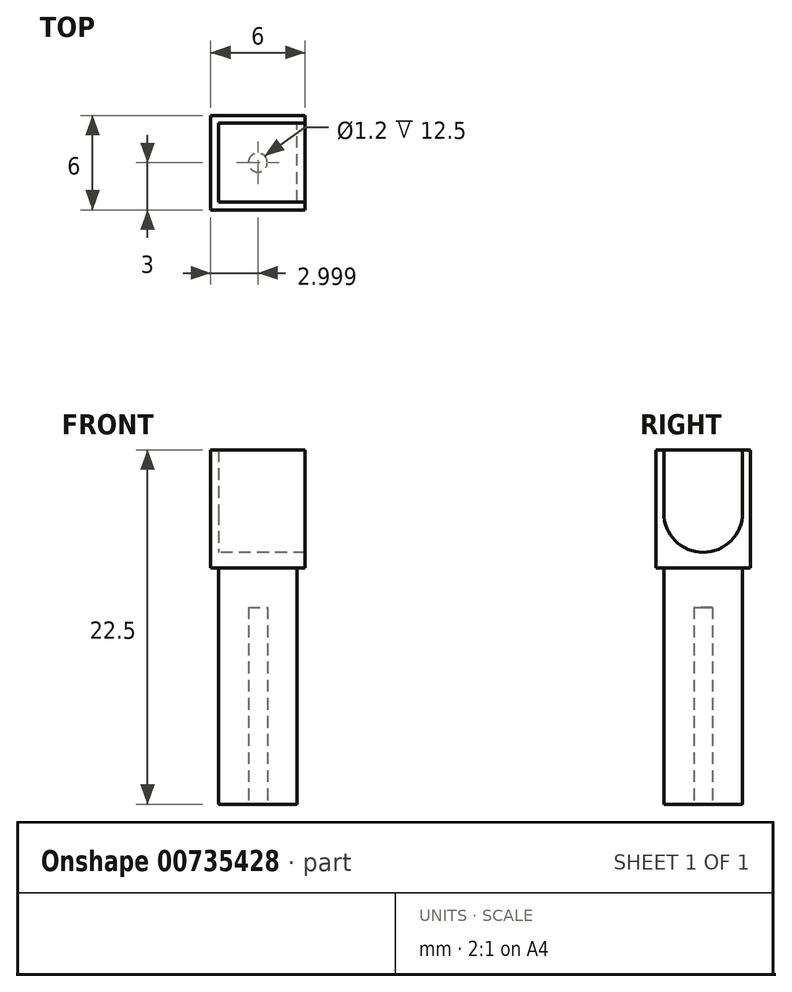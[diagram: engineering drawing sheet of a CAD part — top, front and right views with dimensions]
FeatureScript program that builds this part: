
annotation { "Feature Type Name" : "Feature", "Feature Type Description" : "" }
export const myFeature = defineFeature(function(context is Context, id is Id, definition is map)
    precondition{}
    {
        {
            var Q0;
            Q0=qCreatedBy(makeId("Front.planeOp"),FACE);
            var sketch = newSketch(context, id + "F0", { "sketchPlane" : qUnion([Q0])});
            skLineSegment(sketch, "E0.bottom", {"start": v(-3.25, 14.3) * mm, "end": v(1.75, 14.3) * mm});
            skLineSegment(sketch, "E0.top", {"start": v(-3.25, -8.2) * mm, "end": v(1.75, -8.2) * mm});
            skLineSegment(sketch, "E0.left", {"start": v(-3.25, 14.3) * mm, "end": v(-3.25, -8.2) * mm});
            skLineSegment(sketch, "E0.right", {"start": v(1.75, 14.3) * mm, "end": v(1.75, -8.2) * mm});
            skSolve(sketch);
        }
        {
            var Q0;
            Q0=makeQuery(id+"F0.imprint","IMPRINT",FACE,{"disambiguationData":[TD([[makeQuery(id+"F0.imprint","IMPRINT",EDGE,{"derivedFrom":sQuery(id+"F0.wireOp",EDGE,"E0.bottom")}),-1.0]])]});
            extrude(context, id + "F1", {"entities" : qUnion([Q0]), "depth" : 5 * mm, "offsetDistance" : 25 * mm});
        }
        {
            var Q0;
            Q0=makeQuery(id+"F1.opExtrude","SWEPT_FACE",FACE,{"disambiguationData":[OSD([sQuery(id+"F0.wireOp",EDGE,"E0.top")])]});
            var sketch = newSketch(context, id + "F2", { "sketchPlane" : qUnion([Q0])});
            skCircle(sketch, "E1", {"center": v(-0.75, 2.5) * mm, "radius": 0.6 * mm});
            skPoint(sketch, "E1.centerSnap0", {"position": v(-0.75, 5) * mm});
            skPoint(sketch, "E1.centerSnap1", {"position": v(-3.25, 2.5) * mm});
            skSolve(sketch);
        }
        {
            var Q0;
            Q0=makeQuery(id+"F2.imprint","IMPRINT",FACE,{"disambiguationData":[TD([[makeQuery(id+"F2.imprint","IMPRINT",EDGE,{"derivedFrom":sQuery(id+"F2.wireOp",EDGE,"E1")}),1.0]])]});
            extrude(context, id + "F3", {"entities" : qUnion([Q0]), "operationType" : NewBodyOperationType.REMOVE, "oppositeDirection" : true, "depth" : 20 * mm, "offsetDistance" : 25 * mm});
        }
        {
            var Q0;
            Q0=makeQuery(id+"F1.opExtrude","CAP_FACE",FACE,{"disambiguationData":[OSD([sQuery(id+"F0.wireOp",EDGE,"E0.bottom"),sQuery(id+"F0.wireOp",EDGE,"E0.top"),sQuery(id+"F0.wireOp",EDGE,"E0.left"),sQuery(id+"F0.wireOp",EDGE,"E0.right")])],"isStart":false});
            var sketch = newSketch(context, id + "F4", { "sketchPlane" : qUnion([Q0])});
            skLineSegment(sketch, "E2", {"start": v(-3.25, 14.3) * mm, "end": v(-3.25, 19.3) * mm});
            skLineSegment(sketch, "E3.bottom", {"start": v(-3.25, 19.3) * mm, "end": v(1.75, 19.3) * mm});
            skLineSegment(sketch, "E3.top", {"start": v(-3.25, 14.3) * mm, "end": v(1.75, 14.3) * mm});
            skLineSegment(sketch, "E3.left", {"start": v(-3.25, 19.3) * mm, "end": v(-3.25, 14.3) * mm});
            skLineSegment(sketch, "E3.right", {"start": v(1.75, 19.3) * mm, "end": v(1.75, 14.3) * mm});
            skSolve(sketch);
        }
        {
            var Q0;
            Q0=makeQuery(id+"F4.imprint","IMPRINT",FACE,{"disambiguationData":[TD([[makeQuery(id+"F4.imprint","IMPRINT",EDGE,{"derivedFrom":sQuery(id+"F4.wireOp",EDGE,"E3.bottom")}),-1.0]])]});
            extrude(context, id + "F5", {"entities" : qUnion([Q0]), "operationType" : NewBodyOperationType.ADD, "oppositeDirection" : true, "depth" : 5 * mm, "offsetDistance" : 25 * mm});
        }
        {
            var Q0;
            Q0=makeQuery(id+"F5.boolean.opBoolean","MERGE",FACE,{"derivedFrom":[makeQuery(id+"F1.opExtrude","SWEPT_FACE",FACE,{"disambiguationData":[OSD([sQuery(id+"F0.wireOp",EDGE,"E0.right")])]}),makeQuery(id+"F5.opExtrude","SWEPT_FACE",FACE,{"disambiguationData":[OSD([sQuery(id+"F4.wireOp",EDGE,"E3.right")])]})]});
            var sketch = newSketch(context, id + "F6", { "sketchPlane" : qUnion([Q0])});
            skLineSegment(sketch, "E4", {"start": v(0, 19.3) * mm, "end": v(0, 14.3) * mm});
            skLineSegment(sketch, "E5", {"start": v(0, 14.3) * mm, "end": v(-5, 14.3) * mm});
            skSolve(sketch);
        }
        {
            var Q0;
            Q0=makeQuery(id+"F6.imprint","IMPRINT",FACE,{"disambiguationData":[TD([[makeQuery(id+"F6.imprint","IMPRINT",EDGE,{"derivedFrom":sQuery(id+"F6.wireOp",EDGE,"E4")}),-1.0]])]});
            extrude(context, id + "F7", {"entities" : qUnion([Q0]), "operationType" : NewBodyOperationType.ADD, "depth" : 0.5 * mm, "offsetDistance" : 25 * mm});
        }
        {
            var Q0;
            Q0=makeQuery(id+"F7.boolean.opBoolean","MERGE",FACE,{"derivedFrom":[makeQuery(id+"F5.boolean.opBoolean","MERGE",FACE,{"derivedFrom":[makeQuery(id+"F1.opExtrude","CAP_FACE",FACE,{"disambiguationData":[OSD([sQuery(id+"F0.wireOp",EDGE,"E0.bottom"),sQuery(id+"F0.wireOp",EDGE,"E0.top"),sQuery(id+"F0.wireOp",EDGE,"E0.left"),sQuery(id+"F0.wireOp",EDGE,"E0.right")])],"isStart":true}),makeQuery(id+"F5.opExtrude","CAP_FACE",FACE,{"disambiguationData":[OSD([sQuery(id+"F4.wireOp",EDGE,"E3.bottom"),sQuery(id+"F4.wireOp",EDGE,"E3.top"),sQuery(id+"F4.wireOp",EDGE,"E3.left"),sQuery(id+"F4.wireOp",EDGE,"E3.right")])],"isStart":false})]}),makeQuery(id+"F7.opExtrude","SWEPT_FACE",FACE,{"disambiguationData":[OSD([sQuery(id+"F6.wireOp",EDGE,"E4")])]})]});
            var sketch = newSketch(context, id + "F8", { "sketchPlane" : qUnion([Q0])});
            skLineSegment(sketch, "E6", {"start": v(-1.75, 14.3) * mm, "end": v(3.25, 14.3) * mm});
            skSolve(sketch);
        }
        {
            var Q0;
            {var subQ4=sQuery(id+"F8.wireOp",EDGE,"E6");Q0=makeQuery(id+"F8.imprint","IMPRINT",FACE,{"disambiguationData":[TD([[makeQuery(id+"F8.imprint","IMPRINT",EDGE,{"derivedFrom":subQ4}),1.0]])]});}
            extrude(context, id + "F9", {"entities" : qUnion([Q0]), "operationType" : NewBodyOperationType.ADD, "depth" : 0.5 * mm, "offsetDistance" : 25 * mm});
        }
        {
            var Q0;
            {var subQ0=sQuery(id+"F4.wireOp",EDGE,"E3.right");var subQ1=sQuery(id+"F0.wireOp",EDGE,"E0.right");Q0=makeQuery(id+"F7.boolean.opBoolean","MERGE",FACE,{"derivedFrom":[makeQuery(id+"F5.boolean.opBoolean","MERGE",FACE,{"derivedFrom":[makeQuery(id+"F1.opExtrude","CAP_FACE",FACE,{"disambiguationData":[OSD([sQuery(id+"F0.wireOp",EDGE,"E0.bottom"),sQuery(id+"F0.wireOp",EDGE,"E0.top"),sQuery(id+"F0.wireOp",EDGE,"E0.left"),subQ1])],"isStart":false}),makeQuery(id+"F5.opExtrude","CAP_FACE",FACE,{"disambiguationData":[OSD([sQuery(id+"F4.wireOp",EDGE,"E3.bottom"),sQuery(id+"F4.wireOp",EDGE,"E3.top"),sQuery(id+"F4.wireOp",EDGE,"E3.left"),subQ0])],"isStart":true})]}),makeQuery(id+"F7.opExtrude","SWEPT_FACE",FACE,{"disambiguationData":[OSD([subQ1,subQ0])]})]});}
            var sketch = newSketch(context, id + "F10", { "sketchPlane" : qUnion([Q0])});
            skLineSegment(sketch, "E7", {"start": v(1.75, 14.3) * mm, "end": v(-3.25, 14.3) * mm});
            skSolve(sketch);
        }
        {
            var Q0;
            {var subQ4=sQuery(id+"F10.wireOp",EDGE,"E7");Q0=makeQuery(id+"F10.imprint","IMPRINT",FACE,{"disambiguationData":[TD([[makeQuery(id+"F10.imprint","IMPRINT",EDGE,{"derivedFrom":subQ4}),-1.0]])]});}
            extrude(context, id + "F11", {"entities" : qUnion([Q0]), "operationType" : NewBodyOperationType.ADD, "depth" : 0.5 * mm, "offsetDistance" : 25 * mm});
        }
        {
            var Q0;
            {var subQ0=sQuery(id+"F4.wireOp",EDGE,"E3.left");var subQ1=sQuery(id+"F0.wireOp",EDGE,"E0.left");Q0=makeQuery(id+"F11.boolean.opBoolean","MERGE",FACE,{"derivedFrom":[makeQuery(id+"F9.boolean.opBoolean","MERGE",FACE,{"derivedFrom":[makeQuery(id+"F5.boolean.opBoolean","MERGE",FACE,{"derivedFrom":[makeQuery(id+"F1.opExtrude","SWEPT_FACE",FACE,{"disambiguationData":[OSD([subQ1])]}),makeQuery(id+"F5.opExtrude","SWEPT_FACE",FACE,{"disambiguationData":[OSD([subQ0])]})]}),makeQuery(id+"F9.opExtrude","SWEPT_FACE",FACE,{"disambiguationData":[OSD([subQ1,subQ0])]})]}),makeQuery(id+"F11.opExtrude","SWEPT_FACE",FACE,{"disambiguationData":[OSD([subQ1,subQ0])]})]});}
            var sketch = newSketch(context, id + "F12", { "sketchPlane" : qUnion([Q0])});
            skLineSegment(sketch, "E8", {"start": v(0, 14.3) * mm, "end": v(5, 14.3) * mm});
            skSolve(sketch);
        }
        {
            var Q0;
            Q0=makeQuery(id+"F12.imprint","IMPRINT",FACE,{"disambiguationData":[TD([[makeQuery(id+"F12.imprint","IMPRINT",EDGE,{"derivedFrom":sQuery(id+"F12.wireOp",EDGE,"E8")}),1.0]])]});
            extrude(context, id + "F13", {"entities" : qUnion([Q0]), "operationType" : NewBodyOperationType.ADD, "depth" : 0.5 * mm, "offsetDistance" : 25 * mm});
        }
        {
            var Q0;
            Q0=makeQuery(id+"F13.opExtrude","CAP_FACE",FACE,{"disambiguationData":[OSD([sQuery(id+"F0.wireOp",EDGE,"E0.left"),sQuery(id+"F0.wireOp",EDGE,"E0.right"),sQuery(id+"F4.wireOp",EDGE,"E3.bottom"),sQuery(id+"F4.wireOp",EDGE,"E3.left"),sQuery(id+"F4.wireOp",EDGE,"E3.right"),sQuery(id+"F6.wireOp",EDGE,"E4"),sQuery(id+"F8.wireOp",EDGE,"E6"),sQuery(id+"F10.wireOp",EDGE,"E7"),sQuery(id+"F12.wireOp",EDGE,"E8")])],"isStart":false});
            var sketch = newSketch(context, id + "F14", { "sketchPlane" : qUnion([Q0])});
            skLineSegment(sketch, "E9", {"start": v(0, 17.8) * mm, "end": v(-0.5, 17.8) * mm});
            skLineSegment(sketch, "E10", {"start": v(5, 17.8) * mm, "end": v(5.5, 17.8) * mm});
            skArc(sketch, "E11", {"start": v(0, 17.8) * mm, "mid": v(2.5, 15.3) * mm, "end": v(5, 17.8) * mm});
            skSolve(sketch);
        }
        {
            var Q0;
            {var subQ4=sQuery(id+"F14.wireOp",EDGE,"E9");Q0=makeQuery(id+"F14.imprint","IMPRINT",FACE,{"disambiguationData":[TD([[makeQuery(id+"F14.imprint","IMPRINT",EDGE,{"derivedFrom":subQ4}),-1.0]])]});}
            extrude(context, id + "F15", {"entities" : qUnion([Q0]), "operationType" : NewBodyOperationType.REMOVE, "oppositeDirection" : true, "depth" : 25 * mm, "offsetDistance" : 25 * mm});
        }
        {
            var Q0;
            Q0=makeQuery(id+"F15.boolean.opBoolean","COPY",FACE,{"derivedFrom":makeQuery(id+"F15.opExtrude","SWEPT_FACE",FACE,{"disambiguationData":[OSD([sQuery(id+"F14.wireOp",EDGE,"E10")])]})});
            var Q1;
            Q1=makeQuery(id+"F15.boolean.opBoolean","COPY",FACE,{"derivedFrom":makeQuery(id+"F15.opExtrude","SWEPT_FACE",FACE,{"disambiguationData":[OSD([sQuery(id+"F14.wireOp",EDGE,"E9")])]})});
            extrude(context, id + "F16", {"entities" : qUnion([Q0, Q1]), "operationType" : NewBodyOperationType.ADD, "depth" : 4 * mm, "offsetDistance" : 25 * mm});
        }
        {
            var Q0;
            Q0=makeQuery(id+"F1.opExtrude","SWEPT_FACE",FACE,{"disambiguationData":[OSD([sQuery(id+"F0.wireOp",EDGE,"E0.top")])]});
            extrude(context, id + "F17", {"entities" : qUnion([Q0]), "operationType" : NewBodyOperationType.REMOVE, "oppositeDirection" : true, "depth" : 7.5 * mm, "offsetDistance" : 25 * mm});
        }
        {
            var Q0;
            Q0=makeQuery(id+"F16.boolean.opBoolean","MERGE",FACE,{"derivedFrom":[makeQuery(id+"F13.opExtrude","CAP_FACE",FACE,{"disambiguationData":[OSD([sQuery(id+"F0.wireOp",EDGE,"E0.left"),sQuery(id+"F0.wireOp",EDGE,"E0.right"),sQuery(id+"F4.wireOp",EDGE,"E3.bottom"),sQuery(id+"F4.wireOp",EDGE,"E3.left"),sQuery(id+"F4.wireOp",EDGE,"E3.right"),sQuery(id+"F6.wireOp",EDGE,"E4"),sQuery(id+"F8.wireOp",EDGE,"E6"),sQuery(id+"F10.wireOp",EDGE,"E7"),sQuery(id+"F12.wireOp",EDGE,"E8")])],"isStart":false}),makeQuery(id+"F16.opExtrude","SWEPT_FACE",FACE,{"disambiguationData":[OSD([sQuery(id+"F14.wireOp",EDGE,"E9")])]}),makeQuery(id+"F16.opExtrude","SWEPT_FACE",FACE,{"disambiguationData":[OSD([sQuery(id+"F14.wireOp",EDGE,"E10")])]})]});
            var sketch = newSketch(context, id + "F18", { "sketchPlane" : qUnion([Q0])});
            skLineSegment(sketch, "E12", {"start": v(0, 21.8) * mm, "end": v(5, 21.8) * mm});
            skSolve(sketch);
        }
        {
            var Q0;
            Q0=makeQuery(id+"F18.imprint","IMPRINT",FACE,{"disambiguationData":[TD([[makeQuery(id+"F18.imprint","IMPRINT",EDGE,{"derivedFrom":sQuery(id+"F18.wireOp",EDGE,"E12")}),-1.0]])]});
            extrude(context, id + "F19", {"entities" : qUnion([Q0]), "operationType" : NewBodyOperationType.ADD, "oppositeDirection" : true, "depth" : 0.5 * mm, "offsetDistance" : 25 * mm});
        }
    });
